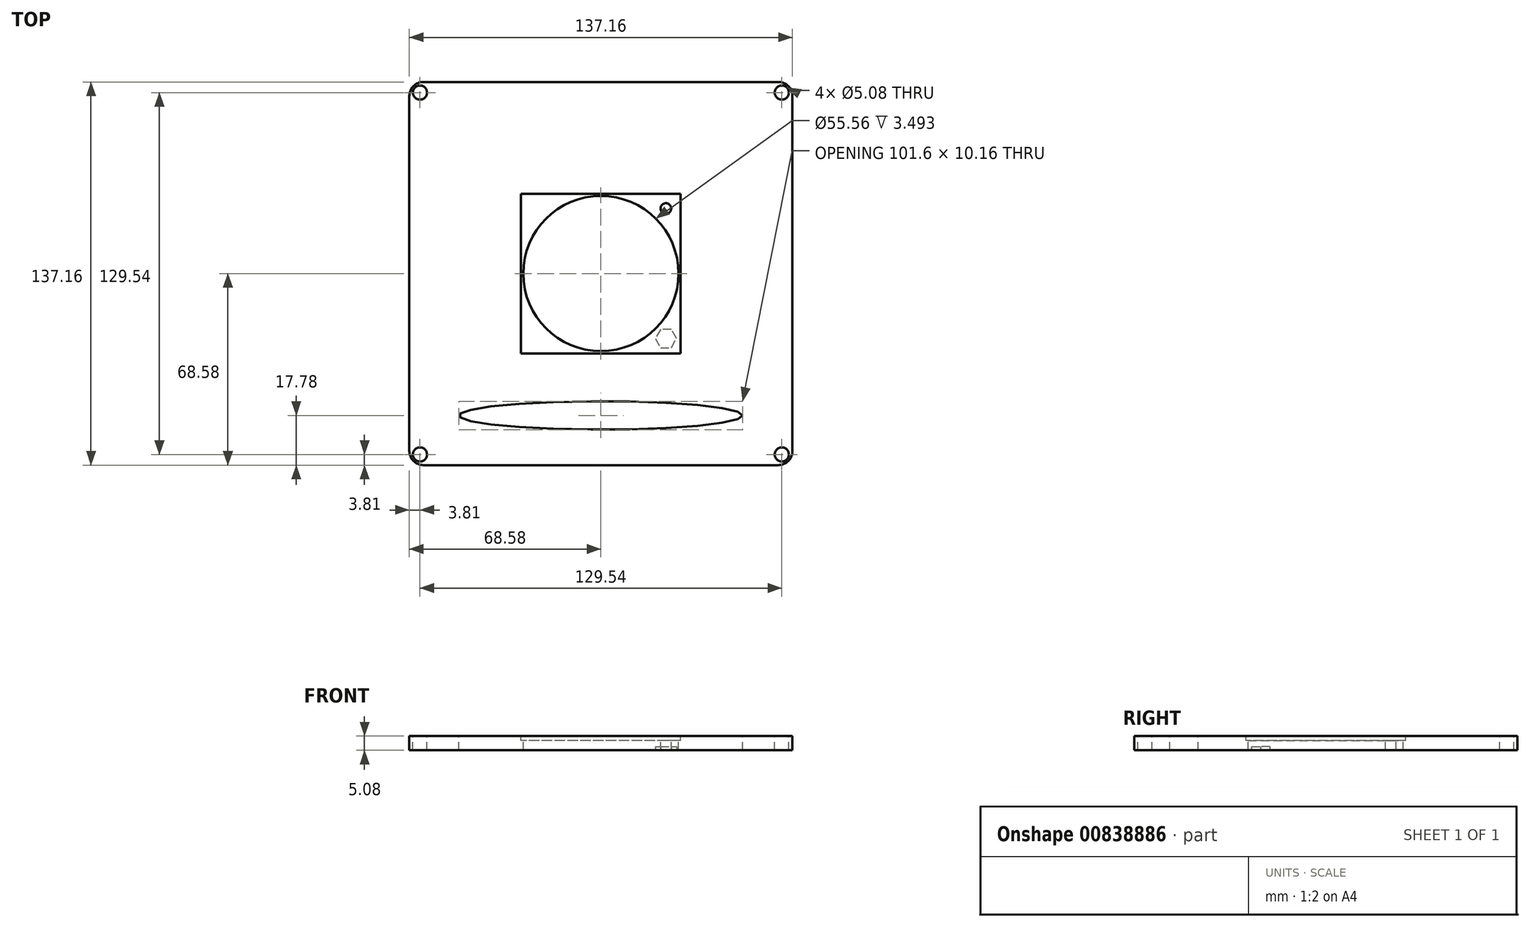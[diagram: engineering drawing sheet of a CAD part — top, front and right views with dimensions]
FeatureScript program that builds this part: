
annotation { "Feature Type Name" : "Feature", "Feature Type Description" : "" }
export const myFeature = defineFeature(function(context is Context, id is Id, definition is map)
    precondition{}
    {
        {
            var Q0;
            Q0=qCreatedBy(makeId("Top.planeOp"),FACE);
            var sketch = newSketch(context, id + "F0", { "sketchPlane" : qUnion([Q0])});
            skLineSegment(sketch, "E0.bottom", {"start": v(68.58, 68.58) * mm, "end": v(-68.58, 68.58) * mm});
            skLineSegment(sketch, "E0.top", {"start": v(68.58, -68.58) * mm, "end": v(-68.58, -68.58) * mm});
            skLineSegment(sketch, "E0.left", {"start": v(68.58, 68.58) * mm, "end": v(68.58, -68.58) * mm});
            skLineSegment(sketch, "E0.right", {"start": v(-68.58, 68.58) * mm, "end": v(-68.58, -68.58) * mm});
            skPoint(sketch, "E0.middle", {"position": v(0, 0) * mm});
            skSolve(sketch);
        }
        {
            var Q0;
            Q0=makeQuery(id+"F0.imprint","IMPRINT",FACE,{"disambiguationData":[TD([[makeQuery(id+"F0.imprint","IMPRINT",EDGE,{"derivedFrom":sQuery(id+"F0.wireOp",EDGE,"E0.bottom")}),1.0]])]});
            extrude(context, id + "F1", {"entities" : qUnion([Q0]), "depth" : 5.08 * mm, "offsetDistance" : 25.4 * mm});
        }
        {
            var Q0;
            Q0=makeQuery(id+"F1.opExtrude","SWEPT_EDGE",EDGE,{"disambiguationData":[OSD([sQuery(id+"F0.wireOp",EDGE,"E0.top"),sQuery(id+"F0.wireOp",EDGE,"E0.right")])]});
            var Q1;
            Q1=makeQuery(id+"F1.opExtrude","SWEPT_EDGE",EDGE,{"disambiguationData":[OSD([sQuery(id+"F0.wireOp",EDGE,"E0.top"),sQuery(id+"F0.wireOp",EDGE,"E0.left")])]});
            var Q2;
            Q2=makeQuery(id+"F1.opExtrude","SWEPT_EDGE",EDGE,{"disambiguationData":[OSD([sQuery(id+"F0.wireOp",EDGE,"E0.bottom"),sQuery(id+"F0.wireOp",EDGE,"E0.left")])]});
            var Q3;
            Q3=makeQuery(id+"F1.opExtrude","SWEPT_EDGE",EDGE,{"disambiguationData":[OSD([sQuery(id+"F0.wireOp",EDGE,"E0.bottom"),sQuery(id+"F0.wireOp",EDGE,"E0.right")])]});
            fillet(context, id + "F2", {"entities" : qUnion([Q0, Q1, Q2, Q3]), "radius" : 5.08 * mm, "tangentPropagation" : true, "allowEdgeOverflow" : false});
        }
        {
            var Q0;
            Q0=makeQuery(id+"F1.opExtrude","CAP_FACE",FACE,{"disambiguationData":[OSD([sQuery(id+"F0.wireOp",EDGE,"E0.bottom"),sQuery(id+"F0.wireOp",EDGE,"E0.top"),sQuery(id+"F0.wireOp",EDGE,"E0.left"),sQuery(id+"F0.wireOp",EDGE,"E0.right")])],"isStart":false});
            var sketch = newSketch(context, id + "F3", { "sketchPlane" : qUnion([Q0])});
            skCircle(sketch, "E1", {"center": v(0, 0) * mm, "radius": 27.78 * mm});
            skSolve(sketch);
        }
        {
            var Q0;
            Q0=qSketchRegion(id+"F3",true);
            var Q1;
            Q1=makeQuery(id+"F1.opExtrude","CAP_FACE",FACE,{"disambiguationData":[OSD([sQuery(id+"F0.wireOp",EDGE,"E0.bottom"),sQuery(id+"F0.wireOp",EDGE,"E0.top"),sQuery(id+"F0.wireOp",EDGE,"E0.left"),sQuery(id+"F0.wireOp",EDGE,"E0.right")])],"isStart":true});
            extrude(context, id + "F4", {"entities" : qUnion([Q0]), "operationType" : NewBodyOperationType.REMOVE, "endBound" : BoundingType.UP_TO_SURFACE, "oppositeDirection" : true, "depth" : 25.4 * mm, "endBoundEntityFace" : qUnion([Q1]), "offsetDistance" : 25.4 * mm});
        }
        {
            var Q0;
            Q0=makeQuery(id+"F1.opExtrude","CAP_FACE",FACE,{"disambiguationData":[OSD([sQuery(id+"F0.wireOp",EDGE,"E0.bottom"),sQuery(id+"F0.wireOp",EDGE,"E0.top"),sQuery(id+"F0.wireOp",EDGE,"E0.left"),sQuery(id+"F0.wireOp",EDGE,"E0.right")])],"isStart":false});
            var sketch = newSketch(context, id + "F5", { "sketchPlane" : qUnion([Q0])});
            skLineSegment(sketch, "E2.bottom", {"start": v(28.58, 28.58) * mm, "end": v(-28.57, 28.58) * mm});
            skLineSegment(sketch, "E2.top", {"start": v(28.57, -28.58) * mm, "end": v(-28.58, -28.58) * mm});
            skLineSegment(sketch, "E2.left", {"start": v(28.58, 28.58) * mm, "end": v(28.57, -28.58) * mm});
            skLineSegment(sketch, "E2.right", {"start": v(-28.57, 28.58) * mm, "end": v(-28.58, -28.58) * mm});
            skPoint(sketch, "E2.middle", {"position": v(0, 0) * mm});
            skSolve(sketch);
        }
        {
            var Q0;
            Q0=qSketchRegion(id+"F5",true);
            extrude(context, id + "F6", {"entities" : qUnion([Q0]), "operationType" : NewBodyOperationType.REMOVE, "oppositeDirection" : true, "depth" : 1.59 * mm, "offsetDistance" : 25.4 * mm});
        }
        {
            var Q0;
            Q0=makeQuery(id+"F6.boolean.opBoolean","COPY",FACE,{"derivedFrom":makeQuery(id+"F6.opExtrude","CAP_FACE",FACE,{"disambiguationData":[OSD([sQuery(id+"F5.wireOp",EDGE,"E2.bottom"),sQuery(id+"F5.wireOp",EDGE,"E2.top"),sQuery(id+"F5.wireOp",EDGE,"E2.left"),sQuery(id+"F5.wireOp",EDGE,"E2.right")])],"isStart":false})});
            var sketch = newSketch(context, id + "F7", { "sketchPlane" : qUnion([Q0])});
            skLineSegment(sketch, "E3", {"start": v(28.58, 28.58) * mm, "end": v(19.64, 19.64) * mm});
            skCircle(sketch, "E4", {"center": v(23.28, 23.28) * mm, "radius": 1.9 * mm});
            skSolve(sketch);
        }
        {
            var Q0;
            {var subQ0=sQuery(id+"F7.wireOp",EDGE,"E4");var subQ1=sQuery(id+"F7.wireOp",EDGE,"E3");var subQ2=makeQuery(id+"F7.imprint","INTERSECT",VERTEX,{"disambiguationData":[OD(0.0)],"derivedFrom":[subQ1,subQ0]});Q0=makeQuery(id+"F7.imprint","IMPRINT",FACE,{"disambiguationData":[TD([[makeQuery(id+"F7.imprint","IMPRINT",EDGE,{"disambiguationData":[TD([[subQ2,1.0]])],"derivedFrom":subQ1}),-1.0]])]});}
            var Q1;
            {var subQ0=sQuery(id+"F7.wireOp",EDGE,"E4");var subQ1=sQuery(id+"F7.wireOp",EDGE,"E3");var subQ2=makeQuery(id+"F7.imprint","INTERSECT",VERTEX,{"disambiguationData":[OD(0.0)],"derivedFrom":[subQ1,subQ0]});Q1=makeQuery(id+"F7.imprint","IMPRINT",FACE,{"disambiguationData":[TD([[makeQuery(id+"F7.imprint","IMPRINT",EDGE,{"disambiguationData":[TD([[subQ2,1.0]])],"derivedFrom":subQ1}),1.0]])]});}
            var Q2;
            Q2=makeQuery(id+"F1.opExtrude","CAP_FACE",FACE,{"disambiguationData":[OSD([sQuery(id+"F0.wireOp",EDGE,"E0.bottom"),sQuery(id+"F0.wireOp",EDGE,"E0.top"),sQuery(id+"F0.wireOp",EDGE,"E0.left"),sQuery(id+"F0.wireOp",EDGE,"E0.right")])],"isStart":true});
            extrude(context, id + "F8", {"entities" : qUnion([Q0, Q1]), "operationType" : NewBodyOperationType.REMOVE, "endBound" : BoundingType.UP_TO_SURFACE, "oppositeDirection" : true, "depth" : 25.4 * mm, "endBoundEntityFace" : qUnion([Q2]), "offsetDistance" : 25.4 * mm});
        }
        {
            var Q0;
            Q0=qCreatedBy(makeId("Front.planeOp"),FACE);
            var sketch = newSketch(context, id + "F9", { "sketchPlane" : qUnion([Q0])});
            skLineSegment(sketch, "E5", {"start": v(0, 79.43) * mm, "end": v(0, -44.4) * mm});
            skSolve(sketch);
        }
        {
            var Q0;
            Q0=makeQuery(id+"F1.opExtrude","CAP_FACE",FACE,{"disambiguationData":[OSD([sQuery(id+"F0.wireOp",EDGE,"E0.bottom"),sQuery(id+"F0.wireOp",EDGE,"E0.top"),sQuery(id+"F0.wireOp",EDGE,"E0.left"),sQuery(id+"F0.wireOp",EDGE,"E0.right")])],"isStart":true});
            var sketch = newSketch(context, id + "F10", { "sketchPlane" : qUnion([Q0])});
            skCircle(sketch, "E6.cCircle", {"center": v(23.28, 23.28) * mm, "radius": 3.3 * mm, "construction": true});
            skLineSegment(sketch, "E6.0", {"start": v(25.18, 26.58) * mm, "end": v(27.09, 23.28) * mm});
            skLineSegment(sketch, "E6.1", {"start": v(27.09, 23.28) * mm, "end": v(25.18, 19.98) * mm});
            skLineSegment(sketch, "E6.2", {"start": v(25.18, 19.98) * mm, "end": v(21.37, 19.98) * mm});
            skLineSegment(sketch, "E6.3", {"start": v(21.37, 19.98) * mm, "end": v(19.47, 23.28) * mm});
            skLineSegment(sketch, "E6.4", {"start": v(19.47, 23.28) * mm, "end": v(21.37, 26.58) * mm});
            skLineSegment(sketch, "E6.5", {"start": v(21.37, 26.58) * mm, "end": v(25.18, 26.58) * mm});
            skPoint(sketch, "E6.0.midPoint", {"position": v(26.13, 24.93) * mm});
            skSolve(sketch);
        }
        {
            var Q0;
            Q0=qSketchRegion(id+"F10",true);
            extrude(context, id + "F11", {"entities" : qUnion([Q0]), "operationType" : NewBodyOperationType.REMOVE, "oppositeDirection" : true, "depth" : 1.27 * mm, "offsetDistance" : 25.4 * mm});
        }
        {
            var Q0;
            Q0=makeQuery(id+"F1.opExtrude","CAP_FACE",FACE,{"disambiguationData":[OSD([sQuery(id+"F0.wireOp",EDGE,"E0.bottom"),sQuery(id+"F0.wireOp",EDGE,"E0.top"),sQuery(id+"F0.wireOp",EDGE,"E0.left"),sQuery(id+"F0.wireOp",EDGE,"E0.right")])],"isStart":false});
            var sketch = newSketch(context, id + "F12", { "sketchPlane" : qUnion([Q0])});
            skLineSegment(sketch, "E7.bottom", {"start": v(64.77, 64.77) * mm, "end": v(-64.77, 64.77) * mm});
            skLineSegment(sketch, "E7.top", {"start": v(64.77, -64.77) * mm, "end": v(-64.77, -64.77) * mm});
            skLineSegment(sketch, "E7.left", {"start": v(64.77, 64.77) * mm, "end": v(64.77, -64.77) * mm});
            skLineSegment(sketch, "E7.right", {"start": v(-64.77, 64.77) * mm, "end": v(-64.77, -64.77) * mm});
            skPoint(sketch, "E7.middle", {"position": v(0, 0) * mm});
            skCircle(sketch, "E8", {"center": v(-64.77, 64.77) * mm, "radius": 2.54 * mm});
            skCircle(sketch, "E9", {"center": v(64.77, 64.77) * mm, "radius": 2.54 * mm});
            skCircle(sketch, "E10", {"center": v(64.77, -64.77) * mm, "radius": 2.54 * mm});
            skCircle(sketch, "E11", {"center": v(-64.77, -64.77) * mm, "radius": 2.54 * mm});
            skSolve(sketch);
        }
        {
            var Q0;
            {var subQ0=sQuery(id+"F12.wireOp",EDGE,"E7.right");var subQ1=sQuery(id+"F12.wireOp",EDGE,"E7.bottom");var subQ2=makeQuery(id+"F12.imprint","INTERSECT",VERTEX,{"derivedFrom":[subQ1,subQ0]});Q0=makeQuery(id+"F12.imprint","IMPRINT",FACE,{"disambiguationData":[TD([[makeQuery(id+"F12.imprint","IMPRINT",EDGE,{"disambiguationData":[TD([[subQ2,1.0]])],"derivedFrom":subQ1}),-1.0]])]});}
            var Q1;
            {var subQ0=sQuery(id+"F12.wireOp",EDGE,"E7.right");var subQ1=sQuery(id+"F12.wireOp",EDGE,"E7.bottom");var subQ2=makeQuery(id+"F12.imprint","INTERSECT",VERTEX,{"derivedFrom":[subQ1,subQ0]});Q1=makeQuery(id+"F12.imprint","IMPRINT",FACE,{"disambiguationData":[TD([[makeQuery(id+"F12.imprint","IMPRINT",EDGE,{"disambiguationData":[TD([[subQ2,1.0]])],"derivedFrom":subQ1}),1.0]])]});}
            var Q2;
            {var subQ0=sQuery(id+"F12.wireOp",EDGE,"E7.right");var subQ1=sQuery(id+"F12.wireOp",EDGE,"E7.top");var subQ2=makeQuery(id+"F12.imprint","INTERSECT",VERTEX,{"derivedFrom":[subQ1,subQ0]});Q2=makeQuery(id+"F12.imprint","IMPRINT",FACE,{"disambiguationData":[TD([[makeQuery(id+"F12.imprint","IMPRINT",EDGE,{"disambiguationData":[TD([[subQ2,1.0]])],"derivedFrom":subQ1}),1.0]])]});}
            var Q3;
            {var subQ0=sQuery(id+"F12.wireOp",EDGE,"E7.right");var subQ1=sQuery(id+"F12.wireOp",EDGE,"E7.top");var subQ2=makeQuery(id+"F12.imprint","INTERSECT",VERTEX,{"derivedFrom":[subQ1,subQ0]});Q3=makeQuery(id+"F12.imprint","IMPRINT",FACE,{"disambiguationData":[TD([[makeQuery(id+"F12.imprint","IMPRINT",EDGE,{"disambiguationData":[TD([[subQ2,1.0]])],"derivedFrom":subQ1}),-1.0]])]});}
            var Q4;
            {var subQ0=sQuery(id+"F12.wireOp",EDGE,"E7.left");var subQ1=sQuery(id+"F12.wireOp",EDGE,"E7.top");var subQ2=makeQuery(id+"F12.imprint","INTERSECT",VERTEX,{"derivedFrom":[subQ1,subQ0]});Q4=makeQuery(id+"F12.imprint","IMPRINT",FACE,{"disambiguationData":[TD([[makeQuery(id+"F12.imprint","IMPRINT",EDGE,{"disambiguationData":[TD([[subQ2,-1.0]])],"derivedFrom":subQ1}),1.0]])]});}
            var Q5;
            {var subQ0=sQuery(id+"F12.wireOp",EDGE,"E7.left");var subQ1=sQuery(id+"F12.wireOp",EDGE,"E7.top");var subQ2=makeQuery(id+"F12.imprint","INTERSECT",VERTEX,{"derivedFrom":[subQ1,subQ0]});Q5=makeQuery(id+"F12.imprint","IMPRINT",FACE,{"disambiguationData":[TD([[makeQuery(id+"F12.imprint","IMPRINT",EDGE,{"disambiguationData":[TD([[subQ2,-1.0]])],"derivedFrom":subQ1}),-1.0]])]});}
            var Q6;
            {var subQ0=sQuery(id+"F12.wireOp",EDGE,"E7.left");var subQ1=sQuery(id+"F12.wireOp",EDGE,"E7.bottom");var subQ2=makeQuery(id+"F12.imprint","INTERSECT",VERTEX,{"derivedFrom":[subQ1,subQ0]});Q6=makeQuery(id+"F12.imprint","IMPRINT",FACE,{"disambiguationData":[TD([[makeQuery(id+"F12.imprint","IMPRINT",EDGE,{"disambiguationData":[TD([[subQ2,-1.0]])],"derivedFrom":subQ1}),1.0]])]});}
            var Q7;
            {var subQ0=sQuery(id+"F12.wireOp",EDGE,"E7.left");var subQ1=sQuery(id+"F12.wireOp",EDGE,"E7.bottom");var subQ2=makeQuery(id+"F12.imprint","INTERSECT",VERTEX,{"derivedFrom":[subQ1,subQ0]});Q7=makeQuery(id+"F12.imprint","IMPRINT",FACE,{"disambiguationData":[TD([[makeQuery(id+"F12.imprint","IMPRINT",EDGE,{"disambiguationData":[TD([[subQ2,-1.0]])],"derivedFrom":subQ1}),-1.0]])]});}
            var Q8;
            Q8=makeQuery(id+"F1.opExtrude","CAP_FACE",FACE,{"disambiguationData":[OSD([sQuery(id+"F0.wireOp",EDGE,"E0.bottom"),sQuery(id+"F0.wireOp",EDGE,"E0.top"),sQuery(id+"F0.wireOp",EDGE,"E0.left"),sQuery(id+"F0.wireOp",EDGE,"E0.right")])],"isStart":true});
            extrude(context, id + "F13", {"entities" : qUnion([Q0, Q1, Q2, Q3, Q4, Q5, Q6, Q7]), "operationType" : NewBodyOperationType.REMOVE, "endBound" : BoundingType.UP_TO_SURFACE, "oppositeDirection" : true, "depth" : 25.4 * mm, "endBoundEntityFace" : qUnion([Q8]), "offsetDistance" : 25.4 * mm});
        }
        {
            var Q0;
            Q0=makeQuery(id+"F1.opExtrude","CAP_FACE",FACE,{"disambiguationData":[OSD([sQuery(id+"F0.wireOp",EDGE,"E0.bottom"),sQuery(id+"F0.wireOp",EDGE,"E0.top"),sQuery(id+"F0.wireOp",EDGE,"E0.left"),sQuery(id+"F0.wireOp",EDGE,"E0.right")])],"isStart":false});
            var sketch = newSketch(context, id + "F14", { "sketchPlane" : qUnion([Q0])});
            skEllipse(sketch, "E12", {"center": v(0, -50.8) * mm, "majorRadius": 50.8 * mm, "minorRadius": 5.08 * mm, "majorAxis": v(1, 0)});
            skSolve(sketch);
        }
        {
            var Q0;
            Q0 = qSketchRegion(id + "F14", true);
            var Q1;
            Q1=makeQuery(id+"F1.opExtrude","CAP_FACE",FACE,{"disambiguationData":[OSD([sQuery(id+"F0.wireOp",EDGE,"E0.bottom"),sQuery(id+"F0.wireOp",EDGE,"E0.top"),sQuery(id+"F0.wireOp",EDGE,"E0.left"),sQuery(id+"F0.wireOp",EDGE,"E0.right")])],"isStart":true});
            extrude(context, id + "F15", {"entities" : qUnion([Q0]), "operationType" : NewBodyOperationType.REMOVE, "endBound" : BoundingType.UP_TO_SURFACE, "oppositeDirection" : true, "depth" : 25.4 * mm, "endBoundEntityFace" : qUnion([Q1]), "offsetDistance" : 25.4 * mm});
        }
    });
